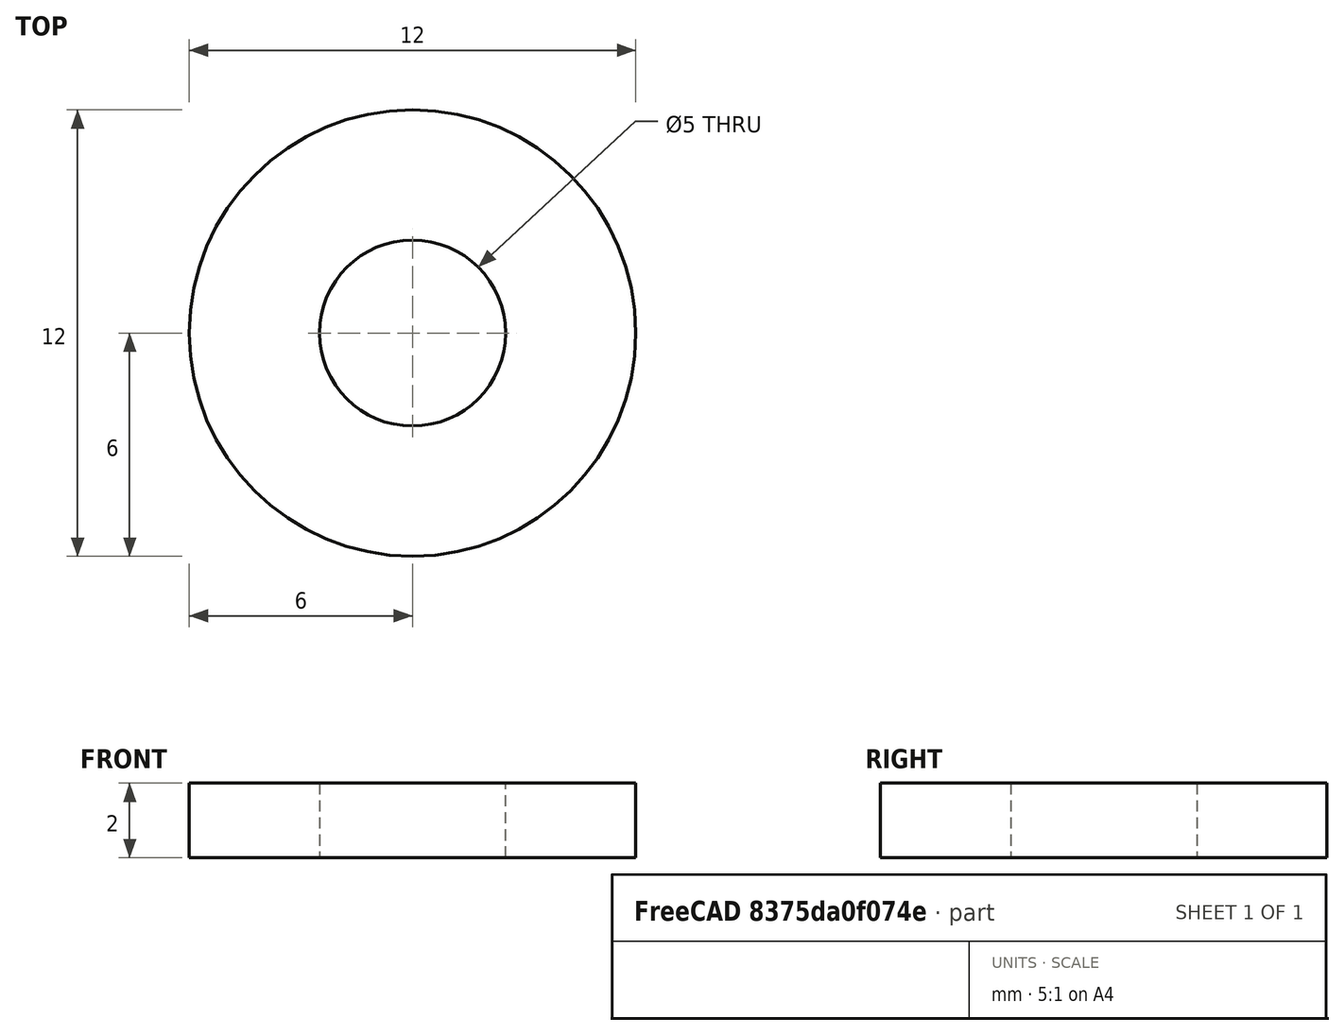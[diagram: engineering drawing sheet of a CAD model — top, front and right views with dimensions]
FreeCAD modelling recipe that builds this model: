
FCSTD DOCUMENT  (FreeCAD 0.19R24276 (Git))
Label: Rolik_4__part_2_print
License: All rights reserved
LicenseURL: http://en.wikipedia.org/wiki/All_rights_reserved
objects: Sketcher::SketchObject×1, PartDesign::Pad×1, PartDesign::Body×1
note: 4 computed .brp shape members not serialized (recipe doc carries the construction recipe); baked Part::Feature solids carry a one-line shape summary decoded from their .brp

FEATURE [Sketcher::SketchObject] Sketch
  FullyConstrained = true
  MapMode = 5
  Support = -> [XY_Plane]
  sketch-geometry (2):
    g0: Circle CenterX=0 CenterY=0 CenterZ=0 NormalX=0 NormalY=0 NormalZ=1 AngleXU=0 Radius=2.5
    g1: Circle CenterX=0 CenterY=0 CenterZ=0 NormalX=0 NormalY=0 NormalZ=1 AngleXU=0 Radius=6
  constraints (4):
    c: Coincident(g0,g-1)
    c: Coincident(g1,g0)
    c: Diameter(g0) = 5
    c: Diameter(g1) = 12
FEATURE [PartDesign::Pad] Pad
  Direction = (1,1,1)
  Length = 2
  Length2 = 100
  Profile = -> Sketch
  Type = 0
FEATURE [PartDesign::Body] Body
  Group = -> [Sketch,Pad]
  Origin = -> Origin
  Tip = -> Pad
